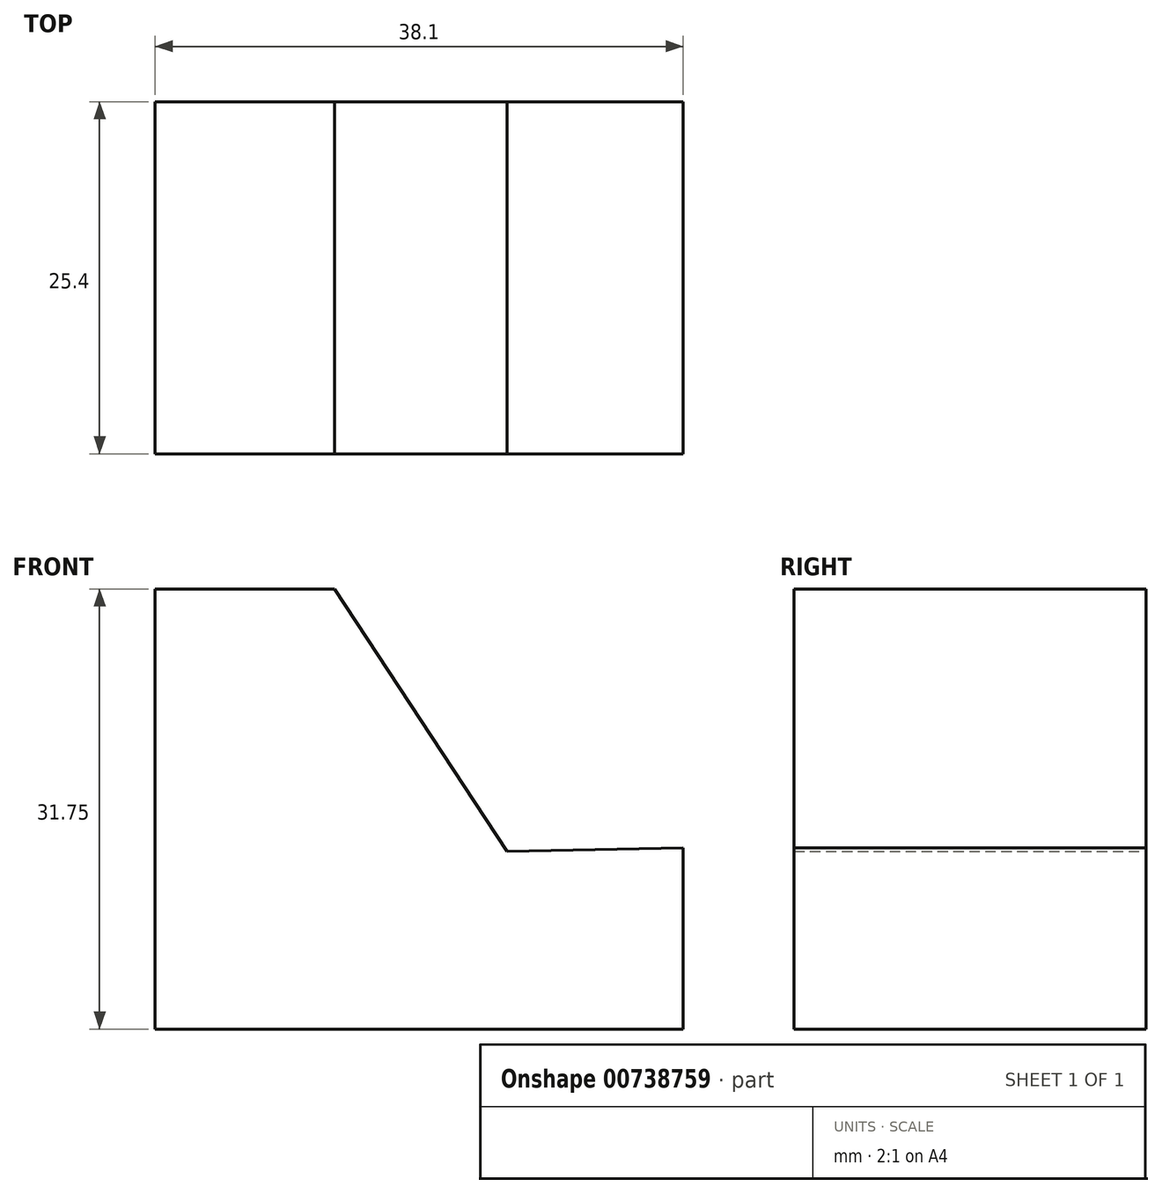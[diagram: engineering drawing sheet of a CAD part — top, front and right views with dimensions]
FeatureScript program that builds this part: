
annotation { "Feature Type Name" : "Feature", "Feature Type Description" : "" }
export const myFeature = defineFeature(function(context is Context, id is Id, definition is map)
    precondition{}
    {
        {
            var Q0;
            Q0=qCreatedBy(makeId("Front.planeOp"),FACE);
            var sketch = newSketch(context, id + "F0", { "sketchPlane" : qUnion([Q0])});
            skLineSegment(sketch, "E0", {"start": v(0, 0) * mm, "end": v(0, 31.75) * mm});
            skLineSegment(sketch, "E1", {"start": v(0, 31.75) * mm, "end": v(-38.1, 31.75) * mm});
            skLineSegment(sketch, "E2", {"start": v(-38.1, 31.75) * mm, "end": v(-38.1, 0) * mm});
            skLineSegment(sketch, "E3", {"start": v(-38.1, 0) * mm, "end": v(0, 0) * mm});
            skSolve(sketch);
        }
        {
            var Q0;
            Q0 = qSketchRegion(id + "F0", true);
            extrude(context, id + "F1", {"entities" : qUnion([Q0]), "depth" : 25.4 * mm, "offsetDistance" : 25.4 * mm});
        }
        {
            var Q0;
            Q0=qCreatedBy(makeId("Front.planeOp"),FACE);
            var sketch = newSketch(context, id + "F2", { "sketchPlane" : qUnion([Q0])});
            skLineSegment(sketch, "E4", {"start": v(0, 13.06) * mm, "end": v(0, 32.11) * mm});
            skLineSegment(sketch, "E5", {"start": v(0, 32.11) * mm, "end": v(-25.4, 32.11) * mm});
            skLineSegment(sketch, "E6", {"start": v(-25.4, 32.11) * mm, "end": v(-12.7, 12.82) * mm});
            skLineSegment(sketch, "E7", {"start": v(-12.7, 12.82) * mm, "end": v(0, 13.06) * mm});
            skSolve(sketch);
        }
        {
            var Q0;
            Q0 = qSketchRegion(id + "F2", true);
            extrude(context, id + "F3", {"entities" : qUnion([Q0]), "operationType" : NewBodyOperationType.REMOVE, "endBound" : BoundingType.THROUGH_ALL, "depth" : 25.4 * mm, "offsetDistance" : 25.4 * mm});
        }
    });
